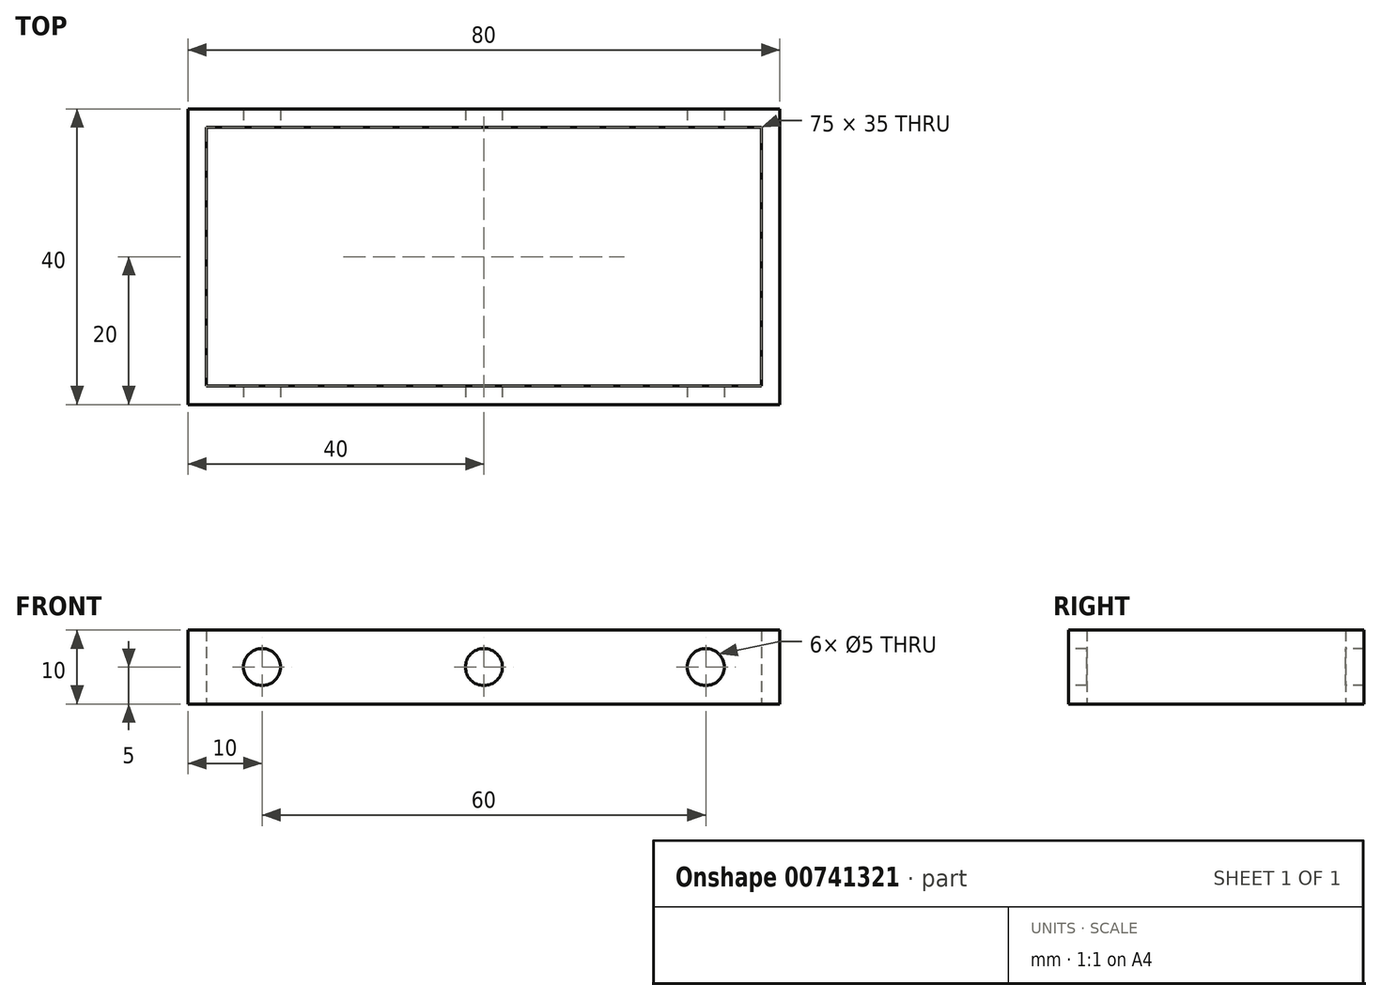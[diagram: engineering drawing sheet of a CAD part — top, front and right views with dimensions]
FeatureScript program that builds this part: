
annotation { "Feature Type Name" : "Feature", "Feature Type Description" : "" }
export const myFeature = defineFeature(function(context is Context, id is Id, definition is map)
    precondition{}
    {
        {
            var Q0;
            Q0=qCreatedBy(makeId("Top.planeOp"),FACE);
            var sketch = newSketch(context, id + "F0", { "sketchPlane" : qUnion([Q0])});
            skLineSegment(sketch, "E0.bottom", {"start": v(40, 20) * mm, "end": v(-40, 20) * mm});
            skLineSegment(sketch, "E0.top", {"start": v(40, -20) * mm, "end": v(-40, -20) * mm});
            skLineSegment(sketch, "E0.left", {"start": v(40, 20) * mm, "end": v(40, -20) * mm});
            skLineSegment(sketch, "E0.right", {"start": v(-40, 20) * mm, "end": v(-40, -20) * mm});
            skPoint(sketch, "E0.middle", {"position": v(0, 0) * mm});
            skLineSegment(sketch, "E1.0", {"start": v(37.5, -17.5) * mm, "end": v(-37.5, -17.5) * mm});
            skLineSegment(sketch, "E1.1", {"start": v(37.5, 17.5) * mm, "end": v(37.5, -17.5) * mm});
            skLineSegment(sketch, "E1.2", {"start": v(37.5, 17.5) * mm, "end": v(-37.5, 17.5) * mm});
            skLineSegment(sketch, "E1.3", {"start": v(-37.5, 17.5) * mm, "end": v(-37.5, -17.5) * mm});
            skSolve(sketch);
        }
        {
            var Q0;
            Q0 = qSketchRegion(id + "F0", true);
            extrude(context, id + "F1", {"entities" : qUnion([Q0]), "depth" : 10 * mm, "offsetDistance" : 25.4 * mm});
        }
        {
            var Q0;
            Q0=makeQuery(id+"F1.opExtrude","SWEPT_FACE",FACE,{"disambiguationData":[OSD([sQuery(id+"F0.wireOp",EDGE,"E0.top")])]});
            var sketch = newSketch(context, id + "F2", { "sketchPlane" : qUnion([Q0])});
            skLineSegment(sketch, "E2", {"start": v(-30, 5) * mm, "end": v(30, 5) * mm, "construction": true});
            skCircle(sketch, "E3", {"center": v(-30, 5) * mm, "radius": 2.5 * mm});
            skCircle(sketch, "E4", {"center": v(0, 5) * mm, "radius": 2.5 * mm});
            skCircle(sketch, "E5", {"center": v(30, 5) * mm, "radius": 2.5 * mm});
            skSolve(sketch);
        }
        {
            var Q0;
            Q0=makeQuery(id+"F2.imprint","IMPRINT",FACE,{"disambiguationData":[TD([[makeQuery(id+"F2.imprint","IMPRINT",EDGE,{"derivedFrom":sQuery(id+"F2.wireOp",EDGE,"E3")}),1.0]])]});
            var Q1;
            Q1=makeQuery(id+"F2.imprint","IMPRINT",FACE,{"disambiguationData":[TD([[makeQuery(id+"F2.imprint","IMPRINT",EDGE,{"derivedFrom":sQuery(id+"F2.wireOp",EDGE,"E4")}),1.0]])]});
            var Q2;
            Q2=makeQuery(id+"F2.imprint","IMPRINT",FACE,{"disambiguationData":[TD([[makeQuery(id+"F2.imprint","IMPRINT",EDGE,{"derivedFrom":sQuery(id+"F2.wireOp",EDGE,"E5")}),1.0]])]});
            extrude(context, id + "F3", {"entities" : qUnion([Q0, Q1, Q2]), "operationType" : NewBodyOperationType.REMOVE, "endBound" : BoundingType.THROUGH_ALL, "oppositeDirection" : true, "depth" : 25.4 * mm, "offsetDistance" : 25.4 * mm});
        }
    });
